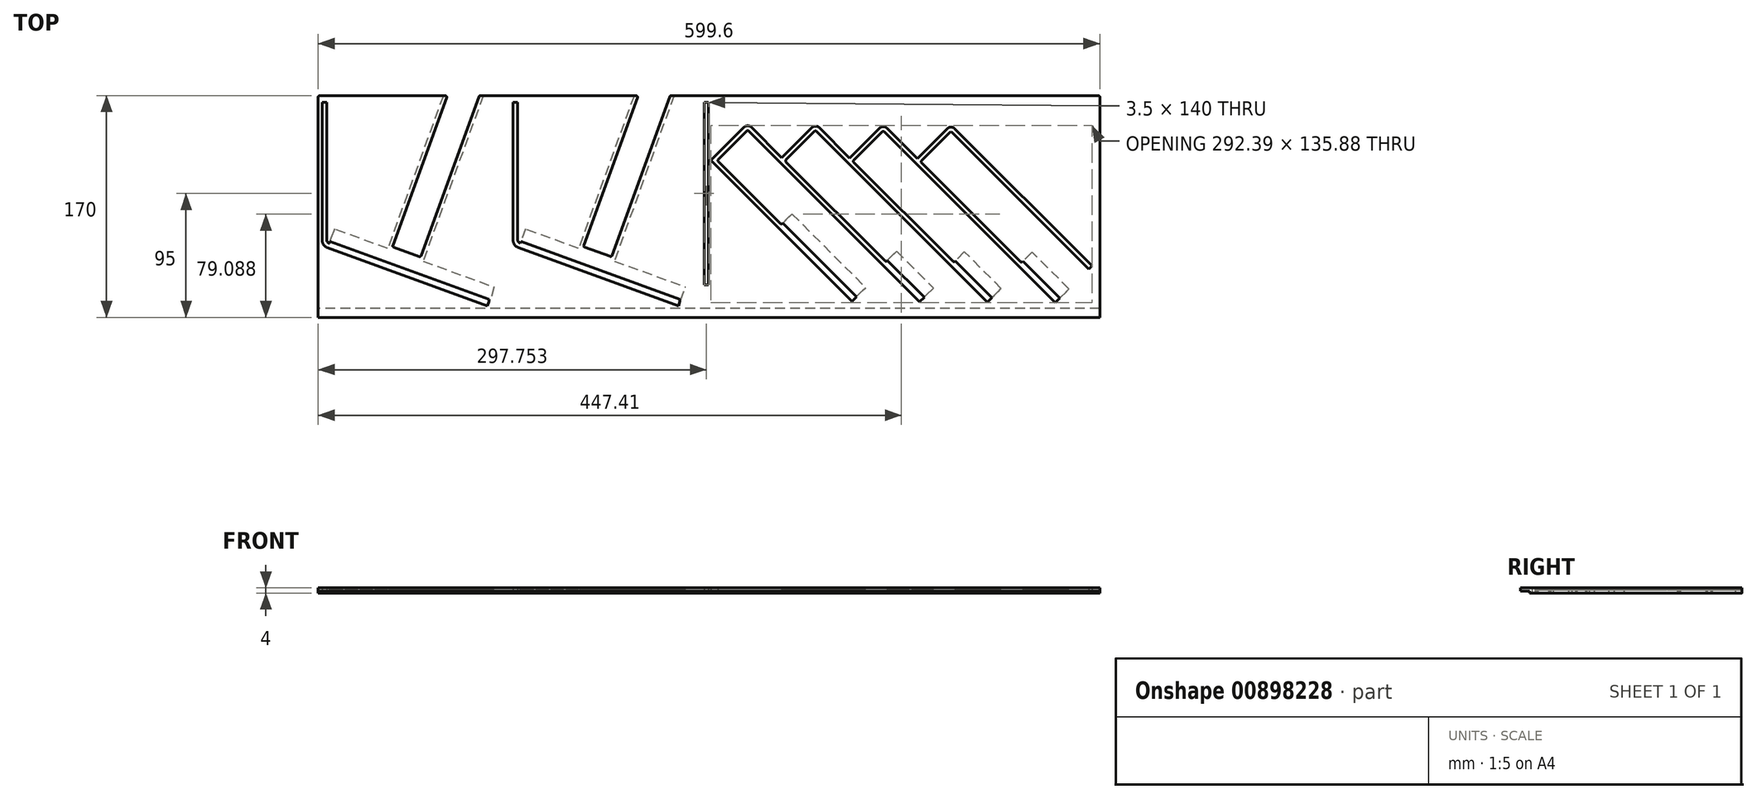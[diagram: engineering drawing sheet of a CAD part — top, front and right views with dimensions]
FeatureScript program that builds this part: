
annotation { "Feature Type Name" : "Feature", "Feature Type Description" : "" }
export const myFeature = defineFeature(function(context is Context, id is Id, definition is map)
    precondition{}
    {
        {
            var Q0;
            Q0=qCreatedBy(makeId("Top.planeOp"),FACE);
            var sketch = newSketch(context, id + "F0", { "sketchPlane" : qUnion([Q0])});
            skLineSegment(sketch, "E0.left", {"start": v(299.43, -88.5) * mm, "end": v(299.43, 80.5) * mm});
            skLineSegment(sketch, "E0.right", {"start": v(-300.17, -88.5) * mm, "end": v(-300.17, 80.5) * mm});
            skPoint(sketch, "E0.middle", {"position": v(0, 0) * mm});
            skLineSegment(sketch, "E1", {"start": v(188.08, 56.3) * mm, "end": v(293.43, -49.07) * mm});
            skLineSegment(sketch, "E2", {"start": v(293.43, -49.07) * mm, "end": v(290.96, -51.54) * mm});
            skLineSegment(sketch, "E3", {"start": v(265.15, -77.35) * mm, "end": v(156.96, 30.84) * mm});
            skLineSegment(sketch, "E4", {"start": v(159.44, 33.31) * mm, "end": v(182.42, 56.3) * mm});
            skLineSegment(sketch, "E5", {"start": v(238.63, -45.88) * mm, "end": v(162.62, 30.13) * mm});
            skLineSegment(sketch, "E6", {"start": v(162.62, 31.54) * mm, "end": v(184.54, 53.46) * mm});
            skLineSegment(sketch, "E7", {"start": v(185.95, 53.46) * mm, "end": v(290.96, -51.54) * mm});
            skLineSegment(sketch, "E8.trimOffspring", {"start": v(267.62, -74.88) * mm, "end": v(265.15, -77.35) * mm});
            skLineSegment(sketch, "E9", {"start": v(136.1, 56.65) * mm, "end": v(159.44, 33.31) * mm});
            skLineSegment(sketch, "E10", {"start": v(213.18, -77) * mm, "end": v(105, 31.2) * mm});
            skLineSegment(sketch, "E11", {"start": v(107.47, 33.67) * mm, "end": v(130.45, 56.65) * mm});
            skLineSegment(sketch, "E12", {"start": v(186.66, -45.53) * mm, "end": v(110.65, 30.48) * mm});
            skLineSegment(sketch, "E13", {"start": v(110.65, 31.9) * mm, "end": v(132.57, 53.82) * mm});
            skLineSegment(sketch, "E14", {"start": v(133.98, 53.82) * mm, "end": v(156.96, 30.84) * mm});
            skLineSegment(sketch, "E15.trimOffspring", {"start": v(215.65, -74.52) * mm, "end": v(213.18, -77) * mm});
            skLineSegment(sketch, "E16", {"start": v(84.13, 57) * mm, "end": v(107.47, 33.67) * mm});
            skLineSegment(sketch, "E17", {"start": v(161.2, -76.64) * mm, "end": v(53.02, 31.54) * mm});
            skLineSegment(sketch, "E18", {"start": v(55.5, 34.02) * mm, "end": v(78.47, 57) * mm});
            skLineSegment(sketch, "E19", {"start": v(134.69, -45.18) * mm, "end": v(58.67, 30.84) * mm});
            skLineSegment(sketch, "E20", {"start": v(58.67, 32.25) * mm, "end": v(80.6, 54.17) * mm});
            skLineSegment(sketch, "E21", {"start": v(82, 54.17) * mm, "end": v(105, 31.2) * mm});
            skLineSegment(sketch, "E22.trimOffspring", {"start": v(163.68, -74.17) * mm, "end": v(161.2, -76.64) * mm});
            skLineSegment(sketch, "E23", {"start": v(32.16, 57.35) * mm, "end": v(55.5, 34.02) * mm});
            skLineSegment(sketch, "E24", {"start": v(109.23, -76.29) * mm, "end": v(1.05, 31.9) * mm});
            skLineSegment(sketch, "E25", {"start": v(1.05, 31.9) * mm, "end": v(26.5, 57.35) * mm});
            skLineSegment(sketch, "E26", {"start": v(54.43, -16.54) * mm, "end": v(6.7, 31.2) * mm});
            skLineSegment(sketch, "E27", {"start": v(6.7, 32.6) * mm, "end": v(28.62, 54.53) * mm});
            skLineSegment(sketch, "E28", {"start": v(30.04, 54.53) * mm, "end": v(53.02, 31.54) * mm});
            skLineSegment(sketch, "E29.trimOffspring", {"start": v(111.7, -73.81) * mm, "end": v(109.23, -76.29) * mm});
            skLineSegment(sketch, "E30", {"start": v(-4.17, 76.5) * mm, "end": v(-4.17, -63.5) * mm});
            skLineSegment(sketch, "E31", {"start": v(-4.17, -63.5) * mm, "end": v(-0.67, -63.5) * mm});
            skLineSegment(sketch, "E32", {"start": v(-0.67, -63.5) * mm, "end": v(-0.67, 76.5) * mm});
            skLineSegment(sketch, "E33", {"start": v(-0.67, 76.5) * mm, "end": v(-4.17, 76.5) * mm});
            skLineSegment(sketch, "E34", {"start": v(-300.17, -88.5) * mm, "end": v(299.43, -88.5) * mm});
            skLineSegment(sketch, "E35", {"start": v(-297.17, 76.5) * mm, "end": v(-297.17, -29.3) * mm});
            skLineSegment(sketch, "E36", {"start": v(-293.22, -34.94) * mm, "end": v(-170.3, -79.67) * mm});
            skLineSegment(sketch, "E37", {"start": v(-170.3, -79.67) * mm, "end": v(-169.11, -76.38) * mm});
            skLineSegment(sketch, "E38", {"start": v(-293.67, -28.95) * mm, "end": v(-293.67, 76.5) * mm});
            skLineSegment(sketch, "E39", {"start": v(-150.67, 76.5) * mm, "end": v(-150.67, -29.3) * mm});
            skLineSegment(sketch, "E40", {"start": v(-146.72, -34.94) * mm, "end": v(-23.8, -79.67) * mm});
            skLineSegment(sketch, "E41", {"start": v(-23.8, -79.67) * mm, "end": v(-22.61, -76.38) * mm});
            skLineSegment(sketch, "E42", {"start": v(-147.17, -28.95) * mm, "end": v(-147.17, 76.5) * mm});
            skPoint(sketch, "E43.orphan", {"position": v(-300.17, -121.36) * mm});
            skPoint(sketch, "E44.orphan", {"position": v(299.43, -122.07) * mm});
            skPoint(sketch, "E45.visualSharp", {"position": v(-147.17, -31.05) * mm});
            skArc(sketch, "E45.filletArc", {"start": v(-147.17, -28.95) * mm, "mid": v(-146.62, -30.67) * mm, "end": v(-145.2, -31.77) * mm});
            skPoint(sketch, "E46.visualSharp", {"position": v(-293.67, -31.05) * mm});
            skArc(sketch, "E46.filletArc", {"start": v(-293.67, -28.95) * mm, "mid": v(-293.12, -30.67) * mm, "end": v(-291.7, -31.77) * mm});
            skPoint(sketch, "E47.visualSharp", {"position": v(-150.67, -33.5) * mm});
            skArc(sketch, "E47.filletArc", {"start": v(-150.67, -29.3) * mm, "mid": v(-149.58, -32.74) * mm, "end": v(-146.72, -34.94) * mm});
            skPoint(sketch, "E48.visualSharp", {"position": v(-297.17, -33.5) * mm});
            skArc(sketch, "E48.filletArc", {"start": v(-297.17, -29.3) * mm, "mid": v(-296.08, -32.74) * mm, "end": v(-293.22, -34.94) * mm});
            skLineSegment(sketch, "E49", {"start": v(267.62, -74.88) * mm, "end": v(268.69, -73.81) * mm});
            skLineSegment(sketch, "E50", {"start": v(268.69, -73.81) * mm, "end": v(240.4, -45.53) * mm});
            skLineSegment(sketch, "E51", {"start": v(240.4, -45.53) * mm, "end": v(240.05, -45.88) * mm});
            skLineSegment(sketch, "E52", {"start": v(215.65, -74.52) * mm, "end": v(216.71, -73.46) * mm});
            skLineSegment(sketch, "E53", {"start": v(216.71, -73.46) * mm, "end": v(188.43, -45.18) * mm});
            skLineSegment(sketch, "E54", {"start": v(188.43, -45.18) * mm, "end": v(188.08, -45.53) * mm});
            skLineSegment(sketch, "E55", {"start": v(163.68, -74.17) * mm, "end": v(164.74, -73.1) * mm});
            skLineSegment(sketch, "E56", {"start": v(164.74, -73.1) * mm, "end": v(136.46, -44.82) * mm});
            skLineSegment(sketch, "E57", {"start": v(136.46, -44.82) * mm, "end": v(136.1, -45.18) * mm});
            skLineSegment(sketch, "E58", {"start": v(111.7, -73.81) * mm, "end": v(112.77, -72.75) * mm});
            skLineSegment(sketch, "E59", {"start": v(112.77, -72.75) * mm, "end": v(56.2, -16.19) * mm});
            skLineSegment(sketch, "E60", {"start": v(56.2, -16.19) * mm, "end": v(55.85, -16.54) * mm});
            skLineSegment(sketch, "E61", {"start": v(-291.7, -31.77) * mm, "end": v(-291.18, -30.36) * mm});
            skLineSegment(sketch, "E62", {"start": v(-291.18, -30.36) * mm, "end": v(-247.95, -46.1) * mm});
            skLineSegment(sketch, "E63", {"start": v(-145.2, -31.77) * mm, "end": v(-144.68, -30.36) * mm});
            skLineSegment(sketch, "E64", {"start": v(-144.68, -30.36) * mm, "end": v(-101.45, -46.1) * mm});
            skPoint(sketch, "E65.visualSharp", {"position": v(29.33, 60.18) * mm});
            skArc(sketch, "E65.filletArc", {"start": v(32.16, 57.35) * mm, "mid": v(29.33, 58.53) * mm, "end": v(26.5, 57.35) * mm});
            skPoint(sketch, "E66.visualSharp", {"position": v(81.3, 59.83) * mm});
            skArc(sketch, "E66.filletArc", {"start": v(84.13, 57) * mm, "mid": v(81.3, 58.17) * mm, "end": v(78.47, 57) * mm});
            skPoint(sketch, "E67.visualSharp", {"position": v(133.27, 59.48) * mm});
            skArc(sketch, "E67.filletArc", {"start": v(136.1, 56.65) * mm, "mid": v(133.27, 57.82) * mm, "end": v(130.45, 56.65) * mm});
            skPoint(sketch, "E68.visualSharp", {"position": v(185.25, 59.12) * mm});
            skArc(sketch, "E68.filletArc", {"start": v(188.08, 56.3) * mm, "mid": v(185.25, 57.46) * mm, "end": v(182.42, 56.3) * mm});
            skPoint(sketch, "E69.visualSharp", {"position": v(6, 31.9) * mm});
            skArc(sketch, "E69.filletArc", {"start": v(6.7, 32.6) * mm, "mid": v(6.4, 31.9) * mm, "end": v(6.7, 31.2) * mm});
            skPoint(sketch, "E70.visualSharp", {"position": v(57.97, 31.54) * mm});
            skArc(sketch, "E70.filletArc", {"start": v(58.67, 32.25) * mm, "mid": v(58.38, 31.54) * mm, "end": v(58.67, 30.84) * mm});
            skPoint(sketch, "E71.visualSharp", {"position": v(109.94, 31.2) * mm});
            skArc(sketch, "E71.filletArc", {"start": v(110.65, 31.9) * mm, "mid": v(110.35, 31.2) * mm, "end": v(110.65, 30.48) * mm});
            skPoint(sketch, "E72.visualSharp", {"position": v(161.91, 30.84) * mm});
            skArc(sketch, "E72.filletArc", {"start": v(162.62, 31.54) * mm, "mid": v(162.33, 30.84) * mm, "end": v(162.62, 30.13) * mm});
            skPoint(sketch, "E73.visualSharp", {"position": v(81.3, 54.88) * mm});
            skArc(sketch, "E73.filletArc", {"start": v(82, 54.17) * mm, "mid": v(81.3, 54.46) * mm, "end": v(80.6, 54.17) * mm});
            skPoint(sketch, "E74.visualSharp", {"position": v(29.33, 55.23) * mm});
            skArc(sketch, "E74.filletArc", {"start": v(30.04, 54.53) * mm, "mid": v(29.33, 54.82) * mm, "end": v(28.62, 54.53) * mm});
            skPoint(sketch, "E75.visualSharp", {"position": v(133.27, 54.53) * mm});
            skArc(sketch, "E75.filletArc", {"start": v(133.98, 53.82) * mm, "mid": v(133.27, 54.11) * mm, "end": v(132.57, 53.82) * mm});
            skPoint(sketch, "E76.visualSharp", {"position": v(185.25, 54.17) * mm});
            skArc(sketch, "E76.filletArc", {"start": v(185.95, 53.46) * mm, "mid": v(185.25, 53.76) * mm, "end": v(184.54, 53.46) * mm});
            skLineSegment(sketch, "E77", {"start": v(-72.5, -58.22) * mm, "end": v(-72.5, -58.22) * mm});
            skLineSegment(sketch, "E78", {"start": v(-242.9, -33.36) * mm, "end": v(-201.58, 80.16) * mm});
            skLineSegment(sketch, "E79", {"start": v(-178.95, 75.11) * mm, "end": v(-221.29, -41.22) * mm});
            skLineSegment(sketch, "E80", {"start": v(-222.57, -41.82) * mm, "end": v(-242.3, -34.64) * mm});
            skLineSegment(sketch, "E81", {"start": v(-96.5, -33.32) * mm, "end": v(-55.2, 80.16) * mm});
            skLineSegment(sketch, "E82", {"start": v(-32.58, 75.09) * mm, "end": v(-74.9, -41.18) * mm});
            skLineSegment(sketch, "E83", {"start": v(-76.18, -41.78) * mm, "end": v(-95.91, -34.6) * mm});
            skLineSegment(sketch, "E84", {"start": v(-299.17, 81.5) * mm, "end": v(-202.52, 81.5) * mm});
            skLineSegment(sketch, "E85", {"start": v(-297.17, 76.5) * mm, "end": v(-293.67, 76.5) * mm});
            skLineSegment(sketch, "E86", {"start": v(-150.67, 76.5) * mm, "end": v(-147.17, 76.5) * mm});
            skLineSegment(sketch, "E87", {"start": v(-178.95, 75.11) * mm, "end": v(-176.86, 80.84) * mm});
            skLineSegment(sketch, "E88", {"start": v(-32.58, 75.09) * mm, "end": v(-30.48, 80.84) * mm});
            skLineSegment(sketch, "E89.trimOffspring", {"start": v(-175.92, 81.5) * mm, "end": v(-56.15, 81.5) * mm});
            skLineSegment(sketch, "E90.trimOffspring", {"start": v(-29.54, 81.5) * mm, "end": v(298.43, 81.5) * mm});
            skPoint(sketch, "E91.visualSharp", {"position": v(-300.17, 81.5) * mm});
            skArc(sketch, "E91.filletArc", {"start": v(-299.17, 81.5) * mm, "mid": v(-299.87, 81.2) * mm, "end": v(-300.17, 80.5) * mm});
            skPoint(sketch, "E92.visualSharp", {"position": v(299.43, 81.5) * mm});
            skArc(sketch, "E92.filletArc", {"start": v(299.43, 80.5) * mm, "mid": v(299.14, 81.2) * mm, "end": v(298.43, 81.5) * mm});
            skPoint(sketch, "E93.visualSharp", {"position": v(-30.24, 81.5) * mm});
            skArc(sketch, "E93.filletArc", {"start": v(-29.54, 81.5) * mm, "mid": v(-30.12, 81.32) * mm, "end": v(-30.48, 80.84) * mm});
            skPoint(sketch, "E94.visualSharp", {"position": v(-54.72, 81.5) * mm});
            skArc(sketch, "E94.filletArc", {"start": v(-55.2, 80.16) * mm, "mid": v(-55.33, 81.07) * mm, "end": v(-56.15, 81.5) * mm});
            skPoint(sketch, "E95.visualSharp", {"position": v(-176.62, 81.5) * mm});
            skArc(sketch, "E95.filletArc", {"start": v(-175.92, 81.5) * mm, "mid": v(-176.5, 81.32) * mm, "end": v(-176.86, 80.84) * mm});
            skPoint(sketch, "E96.visualSharp", {"position": v(-201.1, 81.5) * mm});
            skArc(sketch, "E96.filletArc", {"start": v(-201.58, 80.16) * mm, "mid": v(-201.7, 81.07) * mm, "end": v(-202.52, 81.5) * mm});
            skPoint(sketch, "E97.visualSharp", {"position": v(-101.4, -47.6) * mm});
            skPoint(sketch, "E98.visualSharp", {"position": v(-247.9, -47.6) * mm});
            skLineSegment(sketch, "E99", {"start": v(-247.95, -46.1) * mm, "end": v(-216, -57.72) * mm});
            skLineSegment(sketch, "E100", {"start": v(-101.45, -46.1) * mm, "end": v(-69.5, -57.72) * mm});
            skPoint(sketch, "E101.visualSharp", {"position": v(-75.24, -42.12) * mm});
            skArc(sketch, "E101.filletArc", {"start": v(-76.18, -41.78) * mm, "mid": v(-75.41, -41.75) * mm, "end": v(-74.9, -41.18) * mm});
            skPoint(sketch, "E102.visualSharp", {"position": v(-96.85, -34.26) * mm});
            skArc(sketch, "E102.filletArc", {"start": v(-96.5, -33.32) * mm, "mid": v(-96.47, -34.08) * mm, "end": v(-95.91, -34.6) * mm});
            skPoint(sketch, "E103.visualSharp", {"position": v(-70.02, -59.13) * mm});
            skPoint(sketch, "E104.visualSharp", {"position": v(-221.63, -42.16) * mm});
            skArc(sketch, "E104.filletArc", {"start": v(-222.57, -41.82) * mm, "mid": v(-221.8, -41.79) * mm, "end": v(-221.29, -41.22) * mm});
            skPoint(sketch, "E105.visualSharp", {"position": v(-243.24, -34.3) * mm});
            skArc(sketch, "E105.filletArc", {"start": v(-242.9, -33.36) * mm, "mid": v(-242.87, -34.12) * mm, "end": v(-242.3, -34.64) * mm});
            skPoint(sketch, "E106.visualSharp", {"position": v(-216.52, -59.13) * mm});
            skPoint(sketch, "E107.visualSharp", {"position": v(55.14, -17.25) * mm});
            skArc(sketch, "E107.filletArc", {"start": v(54.43, -16.54) * mm, "mid": v(55.14, -16.83) * mm, "end": v(55.85, -16.54) * mm});
            skPoint(sketch, "E108.visualSharp", {"position": v(135.4, -45.88) * mm});
            skArc(sketch, "E108.filletArc", {"start": v(134.69, -45.18) * mm, "mid": v(135.4, -45.47) * mm, "end": v(136.1, -45.18) * mm});
            skPoint(sketch, "E109.visualSharp", {"position": v(187.37, -46.24) * mm});
            skArc(sketch, "E109.filletArc", {"start": v(186.66, -45.53) * mm, "mid": v(187.37, -45.82) * mm, "end": v(188.08, -45.53) * mm});
            skPoint(sketch, "E110.visualSharp", {"position": v(239.34, -46.6) * mm});
            skArc(sketch, "E110.filletArc", {"start": v(238.63, -45.88) * mm, "mid": v(239.34, -46.18) * mm, "end": v(240.05, -45.88) * mm});
            skLineSegment(sketch, "E111", {"start": v(-216, -57.72) * mm, "end": v(-169.11, -74.79) * mm});
            skLineSegment(sketch, "E112", {"start": v(-169.11, -74.79) * mm, "end": v(-169.11, -76.38) * mm});
            skLineSegment(sketch, "E113", {"start": v(-69.5, -57.72) * mm, "end": v(-22.61, -74.79) * mm});
            skLineSegment(sketch, "E114", {"start": v(-22.61, -74.79) * mm, "end": v(-22.61, -76.38) * mm});
            skSolve(sketch);
        }
        {
            var Q0;
            Q0=qSketchRegion(id+"F0",true);
            extrude(context, id + "F1", {"entities" : qUnion([Q0]), "depth" : 4 * mm});
        }
        {
            var Q0;
            Q0=makeQuery(id+"F1.opExtrude","CAP_FACE",FACE,{"disambiguationData":[OSD([sQuery(id+"F0.wireOp",EDGE,"E0.top"),sQuery(id+"F0.wireOp",EDGE,"E0.left"),sQuery(id+"F0.wireOp",EDGE,"E0.right"),sQuery(id+"F0.wireOp",EDGE,"E1"),sQuery(id+"F0.wireOp",EDGE,"E2"),sQuery(id+"F0.wireOp",EDGE,"E3"),sQuery(id+"F0.wireOp",EDGE,"E4"),sQuery(id+"F0.wireOp",EDGE,"E5"),sQuery(id+"F0.wireOp",EDGE,"E6"),sQuery(id+"F0.wireOp",EDGE,"E7"),sQuery(id+"F0.wireOp",EDGE,"E8.trimOffspring"),sQuery(id+"F0.wireOp",EDGE,"E9"),sQuery(id+"F0.wireOp",EDGE,"E10"),sQuery(id+"F0.wireOp",EDGE,"E11"),sQuery(id+"F0.wireOp",EDGE,"E12"),sQuery(id+"F0.wireOp",EDGE,"E13"),sQuery(id+"F0.wireOp",EDGE,"E14"),sQuery(id+"F0.wireOp",EDGE,"E15.trimOffspring"),sQuery(id+"F0.wireOp",EDGE,"E16"),sQuery(id+"F0.wireOp",EDGE,"E17"),sQuery(id+"F0.wireOp",EDGE,"E18"),sQuery(id+"F0.wireOp",EDGE,"E19"),sQuery(id+"F0.wireOp",EDGE,"E20"),sQuery(id+"F0.wireOp",EDGE,"E21"),sQuery(id+"F0.wireOp",EDGE,"E22.trimOffspring"),sQuery(id+"F0.wireOp",EDGE,"E23"),sQuery(id+"F0.wireOp",EDGE,"E24"),sQuery(id+"F0.wireOp",EDGE,"E25"),sQuery(id+"F0.wireOp",EDGE,"E26"),sQuery(id+"F0.wireOp",EDGE,"E27"),sQuery(id+"F0.wireOp",EDGE,"E28"),sQuery(id+"F0.wireOp",EDGE,"E29.trimOffspring"),sQuery(id+"F0.wireOp",EDGE,"E30"),sQuery(id+"F0.wireOp",EDGE,"E31"),sQuery(id+"F0.wireOp",EDGE,"E32"),sQuery(id+"F0.wireOp",EDGE,"E33"),sQuery(id+"F0.wireOp",EDGE,"E34"),sQuery(id+"F0.wireOp",EDGE,"E35"),sQuery(id+"F0.wireOp",EDGE,"E36"),sQuery(id+"F0.wireOp",EDGE,"E37"),sQuery(id+"F0.wireOp",EDGE,"rMW3URec-0C8R-i97H-GSKa-9mzG0eoT4OPy"),sQuery(id+"F0.wireOp",EDGE,"E38"),sQuery(id+"F0.wireOp",EDGE,"7f4JG1PR-e8fq-IrSw-QAHP-AJHShleLprlO"),sQuery(id+"F0.wireOp",EDGE,"E39"),sQuery(id+"F0.wireOp",EDGE,"E40"),sQuery(id+"F0.wireOp",EDGE,"E41"),sQuery(id+"F0.wireOp",EDGE,"Wq4ZA5YM-xzJ0-yVii-3j4H-AYTGBk09bdcb"),sQuery(id+"F0.wireOp",EDGE,"E42"),sQuery(id+"F0.wireOp",EDGE,"gIA7jmsT-nlDV-00d0-acZ5-NCJ1QFAXyANS")])],"isStart":true});
            var sketch = newSketch(context, id + "F2", { "sketchPlane" : qUnion([Q0])});
            skLineSegment(sketch, "E115", {"start": v(-300.17, 88.5) * mm, "end": v(299.43, 88.5) * mm});
            skLineSegment(sketch, "E116", {"start": v(299.43, 88.5) * mm, "end": v(299.43, 81.5) * mm});
            skLineSegment(sketch, "E117", {"start": v(299.43, 81.5) * mm, "end": v(-300.17, 81.5) * mm});
            skLineSegment(sketch, "E118", {"start": v(-300.17, 81.5) * mm, "end": v(-300.17, 88.5) * mm});
            skLineSegment(sketch, "E119", {"start": v(268.69, 73.81) * mm, "end": v(275.76, 66.74) * mm});
            skLineSegment(sketch, "E120", {"start": v(275.76, 66.74) * mm, "end": v(247.47, 38.46) * mm});
            skLineSegment(sketch, "E121", {"start": v(247.47, 38.46) * mm, "end": v(240.4, 45.53) * mm});
            skLineSegment(sketch, "E122", {"start": v(216.71, 73.46) * mm, "end": v(223.78, 66.39) * mm});
            skLineSegment(sketch, "E123", {"start": v(223.78, 66.39) * mm, "end": v(195.5, 38.1) * mm});
            skLineSegment(sketch, "E124", {"start": v(195.5, 38.1) * mm, "end": v(188.43, 45.18) * mm});
            skLineSegment(sketch, "E125", {"start": v(268.69, 73.81) * mm, "end": v(240.4, 45.53) * mm});
            skLineSegment(sketch, "E126", {"start": v(216.71, 73.46) * mm, "end": v(188.43, 45.18) * mm});
            skLineSegment(sketch, "E127", {"start": v(164.74, 73.1) * mm, "end": v(136.46, 44.82) * mm});
            skLineSegment(sketch, "E128", {"start": v(136.46, 44.82) * mm, "end": v(143.53, 37.75) * mm});
            skLineSegment(sketch, "E129", {"start": v(143.53, 37.75) * mm, "end": v(171.81, 66.04) * mm});
            skLineSegment(sketch, "E130", {"start": v(171.81, 66.04) * mm, "end": v(164.74, 73.1) * mm});
            skLineSegment(sketch, "E131", {"start": v(112.77, 72.75) * mm, "end": v(56.2, 16.19) * mm});
            skLineSegment(sketch, "E132", {"start": v(56.2, 16.19) * mm, "end": v(63.27, 9.11) * mm});
            skLineSegment(sketch, "E133", {"start": v(63.27, 9.11) * mm, "end": v(119.84, 65.68) * mm});
            skLineSegment(sketch, "E134", {"start": v(119.84, 65.68) * mm, "end": v(112.77, 72.75) * mm});
            skLineSegment(sketch, "E135", {"start": v(-1004.52, -17.26) * mm, "end": v(-1004.52, -17.26) * mm});
            skLineSegment(sketch, "E136", {"start": v(-53.13, -84.97) * mm, "end": v(-56.14, -86.07) * mm});
            skLineSegment(sketch, "E137", {"start": v(-56.14, -86.07) * mm, "end": v(-100.43, 35.61) * mm});
            skLineSegment(sketch, "E138", {"start": v(-100.43, 35.61) * mm, "end": v(-141.2, 20.77) * mm});
            skLineSegment(sketch, "E139", {"start": v(-141.2, 20.77) * mm, "end": v(-144.78, 30.64) * mm});
            skLineSegment(sketch, "E140", {"start": v(-26.18, -84.17) * mm, "end": v(-73.04, 45.35) * mm});
            skLineSegment(sketch, "E141", {"start": v(-53.13, -84.97) * mm, "end": v(-96.23, 33.42) * mm});
            skLineSegment(sketch, "E142", {"start": v(-96.23, 33.42) * mm, "end": v(-75.18, 41.08) * mm});
            skLineSegment(sketch, "E143", {"start": v(-199.63, -84.65) * mm, "end": v(-202.64, -85.75) * mm});
            skLineSegment(sketch, "E144", {"start": v(-202.64, -85.75) * mm, "end": v(-246.82, 35.65) * mm});
            skLineSegment(sketch, "E145", {"start": v(-246.82, 35.65) * mm, "end": v(-287.7, 20.77) * mm});
            skLineSegment(sketch, "E146", {"start": v(-287.7, 20.77) * mm, "end": v(-291.28, 30.64) * mm});
            skLineSegment(sketch, "E147", {"start": v(-175.69, -84.94) * mm, "end": v(-172.68, -83.85) * mm});
            skLineSegment(sketch, "E148", {"start": v(-172.68, -83.85) * mm, "end": v(-219.73, 45.44) * mm});
            skLineSegment(sketch, "E149", {"start": v(-199.63, -84.65) * mm, "end": v(-242.72, 33.74) * mm});
            skLineSegment(sketch, "E150", {"start": v(-242.72, 33.74) * mm, "end": v(-221.67, 41.4) * mm});
            skLineSegment(sketch, "E151", {"start": v(-221.67, 41.4) * mm, "end": v(-175.69, -84.94) * mm});
            skLineSegment(sketch, "E152", {"start": v(-73.04, 45.35) * mm, "end": v(-18.42, 65.23) * mm});
            skLineSegment(sketch, "E153", {"start": v(-144.78, 30.64) * mm, "end": v(-21.99, 75.33) * mm});
            skLineSegment(sketch, "E154", {"start": v(-21.99, 75.33) * mm, "end": v(-18.42, 65.23) * mm});
            skLineSegment(sketch, "E155", {"start": v(-291.28, 30.64) * mm, "end": v(-168.21, 75.43) * mm});
            skLineSegment(sketch, "E156", {"start": v(-219.73, 45.44) * mm, "end": v(-165.2, 65.28) * mm});
            skLineSegment(sketch, "E157", {"start": v(-165.2, 65.28) * mm, "end": v(-168.21, 75.43) * mm});
            skLineSegment(sketch, "E158", {"start": v(-75.18, 41.08) * mm, "end": v(-29.2, -85.26) * mm});
            skLineSegment(sketch, "E159", {"start": v(-29.2, -85.26) * mm, "end": v(-26.18, -84.17) * mm});
            skSolve(sketch);
        }
        {
            var Q0;
            Q0=makeQuery(id+"F2.imprint","IMPRINT",FACE,{"disambiguationData":[TD([[makeQuery(id+"F2.imprint","IMPRINT",EDGE,{"derivedFrom":sQuery(id+"F2.wireOp",EDGE,"E119")}),-1.0]])]});
            var Q1;
            Q1=makeQuery(id+"F2.imprint","IMPRINT",FACE,{"disambiguationData":[TD([[makeQuery(id+"F2.imprint","IMPRINT",EDGE,{"derivedFrom":sQuery(id+"F2.wireOp",EDGE,"E122")}),-1.0]])]});
            var Q2;
            Q2=makeQuery(id+"F2.imprint","IMPRINT",FACE,{"disambiguationData":[TD([[makeQuery(id+"F2.imprint","IMPRINT",EDGE,{"derivedFrom":sQuery(id+"F2.wireOp",EDGE,"E127")}),1.0]])]});
            var Q3;
            Q3=makeQuery(id+"F2.imprint","IMPRINT",FACE,{"disambiguationData":[TD([[makeQuery(id+"F2.imprint","IMPRINT",EDGE,{"derivedFrom":sQuery(id+"F2.wireOp",EDGE,"E131")}),1.0]])]});
            var Q4;
            {var subQ1=sQuery(id+"F2.wireOp",EDGE,"8fb6a346-390b-43d0-a156-07e60583d9f8");Q4=makeQuery(id+"F2.imprint","IMPRINT",FACE,{"disambiguationData":[TD([[makeQuery(id+"F2.imprint","IMPRINT",EDGE,{"derivedFrom":subQ1}),1.0]])]});}
            var Q5;
            {var subQ0=sQuery(id+"F2.wireOp",EDGE,"E136");Q5=makeQuery(id+"F2.imprint","IMPRINT",FACE,{"disambiguationData":[TD([[makeQuery(id+"F2.imprint","IMPRINT",EDGE,{"derivedFrom":subQ0}),-1.0]])]});}
            var Q6;
            {var subQ0=sQuery(id+"F2.wireOp",EDGE,"52c0a096-720d-4815-b4a1-1140e2bbf7f8");Q6=makeQuery(id+"F2.imprint","IMPRINT",FACE,{"disambiguationData":[TD([[makeQuery(id+"F2.imprint","IMPRINT",EDGE,{"derivedFrom":subQ0}),1.0]])]});}
            var Q7;
            {var subQ6=sQuery(id+"F2.wireOp",EDGE,"a6810e08-8d53-41db-9dac-b19748a4023a");Q7=makeQuery(id+"F2.imprint","IMPRINT",FACE,{"disambiguationData":[TD([[makeQuery(id+"F2.imprint","IMPRINT",EDGE,{"derivedFrom":subQ6}),-1.0]])]});}
            var Q8;
            {var subQ1=sQuery(id+"F2.wireOp",EDGE,"E138");Q8=makeQuery(id+"F2.imprint","IMPRINT",FACE,{"disambiguationData":[TD([[makeQuery(id+"F2.imprint","IMPRINT",EDGE,{"derivedFrom":subQ1}),-1.0]])]});}
            var Q9;
            {var subQ8=sQuery(id+"F2.wireOp",EDGE,"5a9c356d-3bd6-4c7f-bf7b-0702d958a0c5");Q9=makeQuery(id+"F2.imprint","IMPRINT",FACE,{"disambiguationData":[TD([[makeQuery(id+"F2.imprint","IMPRINT",EDGE,{"derivedFrom":subQ8}),-1.0]])]});}
            var Q10;
            {var subQ7=sQuery(id+"F2.wireOp",EDGE,"E145");Q10=makeQuery(id+"F2.imprint","IMPRINT",FACE,{"disambiguationData":[TD([[makeQuery(id+"F2.imprint","IMPRINT",EDGE,{"derivedFrom":subQ7}),-1.0]])]});}
            extrude(context, id + "F3", {"entities" : qUnion([Q0, Q1, Q2, Q3, Q4, Q5, Q6, Q7, Q8, Q9, Q10]), "operationType" : NewBodyOperationType.REMOVE, "oppositeDirection" : true, "depth" : 2.5 * mm});
        }
        {
            var Q0;
            Q0=makeQuery(id+"F2.imprint","IMPRINT",FACE,{"disambiguationData":[TD([[makeQuery(id+"F2.imprint","IMPRINT",EDGE,{"derivedFrom":sQuery(id+"F2.wireOp",EDGE,"E115")}),-1.0]])]});
            extrude(context, id + "F4", {"entities" : qUnion([Q0]), "operationType" : NewBodyOperationType.REMOVE, "oppositeDirection" : true, "depth" : 1.5 * mm});
        }
    });
